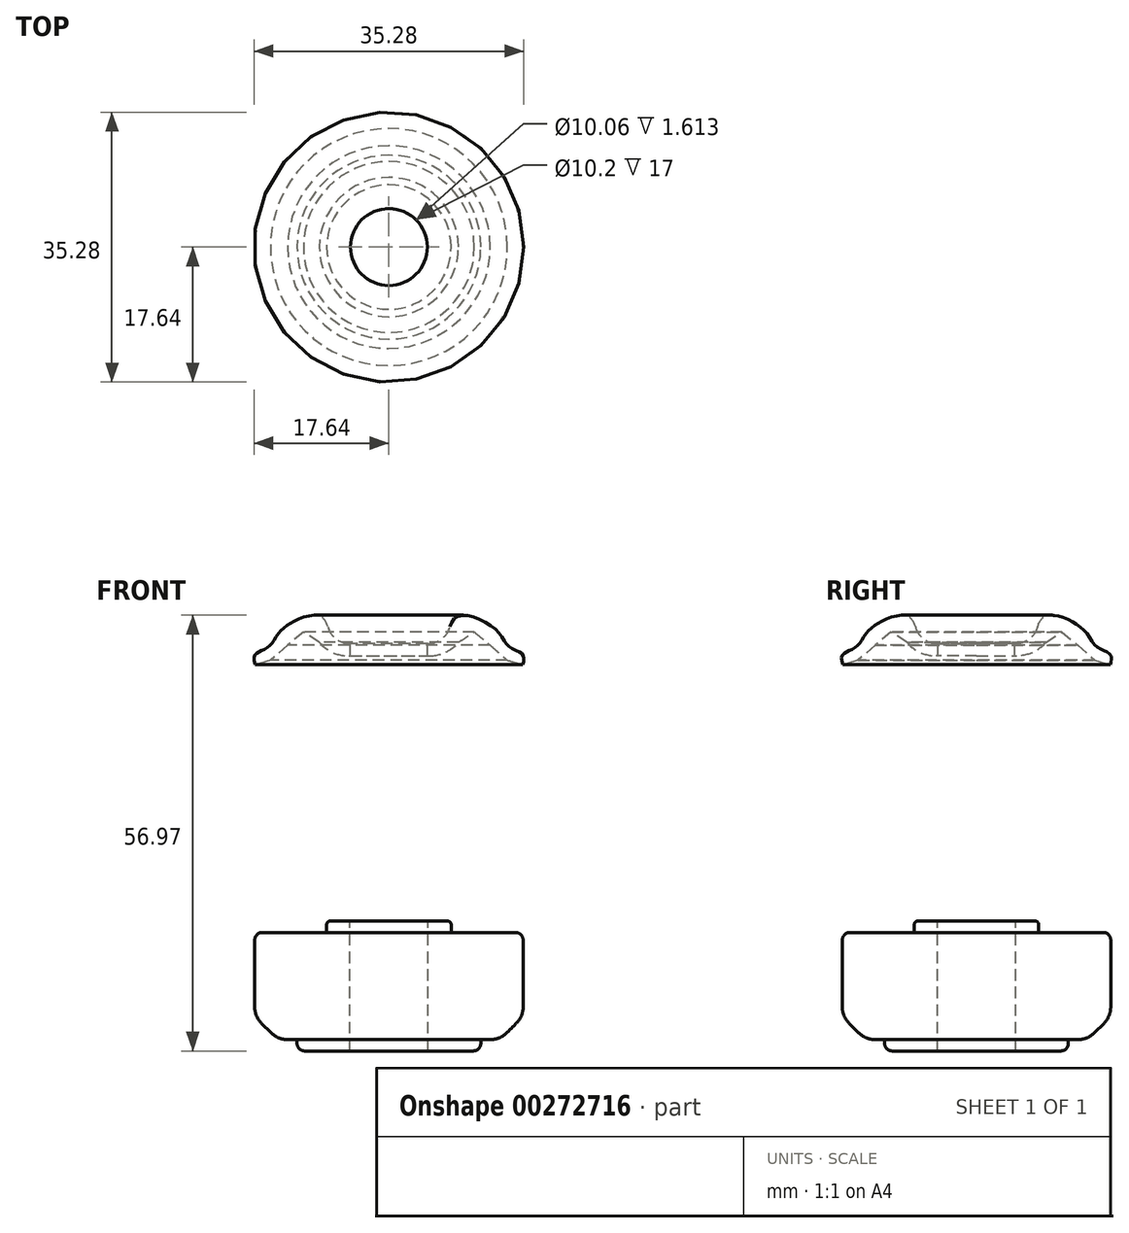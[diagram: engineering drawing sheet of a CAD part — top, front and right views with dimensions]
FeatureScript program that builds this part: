
annotation { "Feature Type Name" : "Feature", "Feature Type Description" : "" }
export const myFeature = defineFeature(function(context is Context, id is Id, definition is map)
    precondition{}
    {
        {
            var Q0;
            Q0=qCreatedBy(makeId("Top.planeOp"),FACE);
            var sketch = newSketch(context, id + "F0", { "sketchPlane" : qUnion([Q0])});
            skCircle(sketch, "E0", {"center": v(0, 0) * mm, "radius": 17.54 * mm});
            skSolve(sketch);
        }
        {
            var Q0;
            Q0=makeQuery(id+"F0.imprint","IMPRINT",FACE,{"disambiguationData":[TD([[makeQuery(id+"F0.imprint","IMPRINT",EDGE,{"derivedFrom":sQuery(id+"F0.wireOp",EDGE,"E0")}),1.0]])]});
            extrude(context, id + "F1", {"entities" : qUnion([Q0]), "depth" : 14 * mm});
        }
        {
            var Q0;
            Q0=makeQuery(id+"F1.opExtrude","CAP_FACE",FACE,{"disambiguationData":[OSD([sQuery(id+"F0.wireOp",EDGE,"E0")])],"isStart":true});
            var sketch = newSketch(context, id + "F2", { "sketchPlane" : qUnion([Q0])});
            skCircle(sketch, "E1", {"center": v(0, 0) * mm, "radius": 12.01 * mm});
            skSolve(sketch);
        }
        {
            var Q0;
            Q0=makeQuery(id+"F2.imprint","IMPRINT",FACE,{"disambiguationData":[TD([[makeQuery(id+"F2.imprint","IMPRINT",EDGE,{"derivedFrom":sQuery(id+"F2.wireOp",EDGE,"E1")}),1.0]])]});
            extrude(context, id + "F3", {"entities" : qUnion([Q0]), "operationType" : NewBodyOperationType.ADD, "depth" : 1.5 * mm});
        }
        {
            var Q0;
            Q0=makeQuery(id+"F1.opExtrude","CAP_FACE",FACE,{"disambiguationData":[OSD([sQuery(id+"F0.wireOp",EDGE,"E0")])],"isStart":false});
            var sketch = newSketch(context, id + "F4", { "sketchPlane" : qUnion([Q0])});
            skCircle(sketch, "E2", {"center": v(0, 0) * mm, "radius": 8.14 * mm});
            skSolve(sketch);
        }
        {
            var Q0;
            Q0=makeQuery(id+"F4.imprint","IMPRINT",FACE,{"disambiguationData":[TD([[makeQuery(id+"F4.imprint","IMPRINT",EDGE,{"derivedFrom":sQuery(id+"F4.wireOp",EDGE,"E2")}),1.0]])]});
            extrude(context, id + "F5", {"entities" : qUnion([Q0]), "operationType" : NewBodyOperationType.ADD, "depth" : 1.5 * mm});
        }
        {
            var Q0;
            Q0=makeQuery(id+"F5.opExtrude","CAP_FACE",FACE,{"disambiguationData":[OSD([sQuery(id+"F4.wireOp",EDGE,"E2")])],"isStart":false});
            var sketch = newSketch(context, id + "F6", { "sketchPlane" : qUnion([Q0])});
            skCircle(sketch, "E3", {"center": v(0, 0) * mm, "radius": 5.1 * mm});
            skSolve(sketch);
        }
        {
            var Q0;
            Q0=makeQuery(id+"F6.imprint","IMPRINT",FACE,{"disambiguationData":[TD([[makeQuery(id+"F6.imprint","IMPRINT",EDGE,{"derivedFrom":sQuery(id+"F6.wireOp",EDGE,"E3")}),1.0]])]});
            extrude(context, id + "F7", {"entities" : qUnion([Q0]), "operationType" : NewBodyOperationType.REMOVE, "oppositeDirection" : true, "depth" : 25 * mm});
        }
        {
            var Q0;
            Q0=makeQuery(id+"F1.opExtrude","CAP_EDGE",EDGE,{"disambiguationData":[OSD([sQuery(id+"F0.wireOp",EDGE,"E0")])],"isStart":true});
            chamfer(context, id + "F8", {"entities" : qUnion([Q0]), "width" : 3 * mm, "tangentPropagation" : true});
        }
        {
            var Q0;
            Q0=makeQuery(id+"F8.opChamfer","BLEND_FACE",FACE,{"disambiguationData":[OSD([sQuery(id+"F0.wireOp",EDGE,"E0")])]});
            fillet(context, id + "F9", {"entities" : qUnion([Q0]), "radius" : 3 * mm, "tangentPropagation" : true, "allowEdgeOverflow" : false});
        }
        {
            var Q0;
            Q0=makeQuery(id+"F1.opExtrude","CAP_EDGE",EDGE,{"disambiguationData":[OSD([sQuery(id+"F0.wireOp",EDGE,"E0")])],"isStart":false});
            var Q1;
            Q1=makeQuery(id+"F3.opExtrude","CAP_EDGE",EDGE,{"disambiguationData":[OSD([sQuery(id+"F2.wireOp",EDGE,"E1")])],"isStart":false});
            fillet(context, id + "F10", {"entities" : qUnion([Q0, Q1]), "radius" : 1 * mm, "tangentPropagation" : true, "allowEdgeOverflow" : false});
        }
        {
            var Q0;
            Q0=makeQuery(id+"F5.opExtrude","CAP_EDGE",EDGE,{"disambiguationData":[OSD([sQuery(id+"F4.wireOp",EDGE,"E2")])],"isStart":false});
            fillet(context, id + "F11", {"entities" : qUnion([Q0]), "radius" : .5 * mm, "tangentPropagation" : true, "allowEdgeOverflow" : false});
        }
        {
            var Q0;
            Q0=qCreatedBy(makeId("Front.planeOp"),FACE);
            var sketch = newSketch(context, id + "F12", { "sketchPlane" : qUnion([Q0])});
            skLineSegment(sketch, "E4", {"start": v(0, 51.77) * mm, "end": v(7.66, 51.77) * mm});
            skPoint(sketch, "E5", {"position": v(17.5, 50.34) * mm});
            skPoint(sketch, "E6", {"position": v(9, 55.34) * mm});
            skFitSpline(sketch, "E7", {"points": [v(7.66, 51.77) * mm, v(9, 55.34) * mm, v(13.88, 53.67) * mm, v(15.78, 51.3) * mm, v(17.5, 50.34) * mm, v(17.5, 49) * mm], "startDerivative": vector(1.96, 20.54) * mm, "endDerivative": vector(-2.76, -11.14) * mm});
            skLineSegment(sketch, "E8", {"start": v(17.5, 49) * mm, "end": v(15.5, 49.58) * mm});
            skLineSegment(sketch, "E9", {"start": v(15.5, 49.58) * mm, "end": v(13.24, 51.54) * mm});
            skLineSegment(sketch, "E10", {"start": v(13.24, 51.54) * mm, "end": v(11.17, 53.26) * mm});
            skLineSegment(sketch, "E11", {"start": v(11.17, 53.26) * mm, "end": v(9.1, 51.94) * mm});
            skLineSegment(sketch, "E12", {"start": v(9.1, 51.94) * mm, "end": v(8.63, 50.15) * mm});
            skLineSegment(sketch, "E13", {"start": v(8.63, 50.15) * mm, "end": v(0, 50.15) * mm});
            skLineSegment(sketch, "E14", {"start": v(0, 50.15) * mm, "end": v(0, 51.77) * mm});
            skLineSegment(sketch, "E15", {"start": v(0, 67.78) * mm, "end": v(0, 39.44) * mm, "construction": true});
            skSolve(sketch);
        }
        {
            var Q0;
            Q0=makeQuery(id+"F12.imprint","IMPRINT",FACE,{"disambiguationData":[TD([[makeQuery(id+"F12.imprint","IMPRINT",EDGE,{"derivedFrom":sQuery(id+"F12.wireOp",EDGE,"E4")}),-1.0]])]});
            var Q1;
            Q1=sQuery(id+"F12.wireOp",EDGE,"E15");
            revolve(context, id + "F13", {"entities" : qUnion([Q0]), "axis" : qUnion([Q1]), "revolveType" : RevolveType.FULL});
        }
        {
            var Q0;
            Q0=makeQuery(id+"F13.opRevolve","SWEPT_EDGE",EDGE,{"disambiguationData":[OSD([sQuery(id+"F12.wireOp",EDGE,"E4"),sQuery(id+"F12.wireOp",EDGE,"E7")])]});
            fillet(context, id + "F14", {"entities" : qUnion([Q0]), "radius" : 3 * mm, "tangentPropagation" : true, "allowEdgeOverflow" : false});
        }
        {
            var Q0;
            Q0=makeQuery(id+"F13.opRevolve","SWEPT_EDGE",EDGE,{"disambiguationData":[OSD([sQuery(id+"F12.wireOp",EDGE,"E12"),sQuery(id+"F12.wireOp",EDGE,"E13")])]});
            fillet(context, id + "F15", {"entities" : qUnion([Q0]), "radius" : 5 * mm, "tangentPropagation" : true, "allowEdgeOverflow" : false});
        }
        {
            var Q0;
            Q0=makeQuery(id+"F13.opRevolve","SWEPT_FACE",FACE,{"disambiguationData":[OSD([sQuery(id+"F12.wireOp",EDGE,"E4")])]});
            var sketch = newSketch(context, id + "F16", { "sketchPlane" : qUnion([Q0])});
            skCircle(sketch, "E16", {"center": v(0, 0) * mm, "radius": 5.03 * mm});
            skSolve(sketch);
        }
        {
            var Q0;
            Q0 = qSketchRegion(id + "F16", true);
            extrude(context, id + "F17", {"entities" : qUnion([Q0]), "operationType" : NewBodyOperationType.REMOVE, "oppositeDirection" : true, "depth" : 20 * mm});
        }
    });
